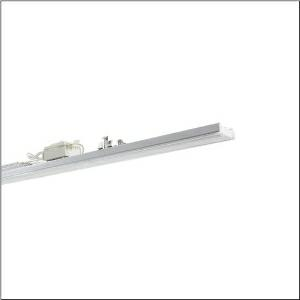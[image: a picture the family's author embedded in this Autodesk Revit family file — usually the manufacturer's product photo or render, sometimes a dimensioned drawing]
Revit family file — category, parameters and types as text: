
# Revit family: licross_21_recessed_mo_52tl127n44xg
name_source: partatom
category: Lighting Fixtures
units: mm (PartAtom-declared; Revit-internal decimal feet)

## family parameters
Cut with Voids When Loaded = No
Host = Face
Light Source = No
Part Type = Normal
Room Calculation Point = No
Round Connector Dimension = Use Diameter
Shared = No

## types (1)
- Licross 21 Recessed MO (1 x LED, 4160 lm, 22.2 W, 4000K)
    Apparent Load = 22 VA
    CIE Flux Codes = 72 92 99 100 100
    Color Rendering = 80
    Color Temperature = 4000K
    Default Elevation = 1800 mm
    Description = Licross 21 Recessed MO, luminaire insert, of sheet steel, galvanised, coil coated, white, length: 1.500mm, width: 66mm, height: 67mm, LED rated luminous flux: 4.160lm, light colour: 840, SDCM (Standard Deviation of Colour Matching)MacAdam ≤ 3 SDCM (initial), control gear: ON/OFF, with plug, 3-pole, with phase selection, mains connection: 220..240V, AC, 50/60Hz, rated input power: 22W, internal wiring halogen-free, primary optical cover: cover, of PMMA, light emission: direct distribution, primary light characteristic: symmetric, protection rating (complete): IP40, insulation class (complete): insulation class I (protective earthing), certification: CE, ENEC, VDE, UKCA, protection symbol: D if used in an environment without relevant dust loads with corresponding accessories, impact resistance: IK06, permissible ambient temperature for indoor applications: -35..+50°C, corresponds to IFS (International Featured Standards) requirements for safety and quality in the food industry, reducing of maximum allowable ambient temperature of 5°C with ceiling mounting, LABS conformity tested according to VDMA 24364:2018-05, The light source and the operating device comply with the requirements of the Ecodesign Regulation (EU) 2019/2020 and are replaceable in accordance with this regulation, packaging unit: 1 piece
    Height = 58 mm
    Lamp = 1 x LED
    Lamp Light Flux = 4160 lm
    Lamp Power = 22.2 W
    Lamp count = 1
    Length = 1500 mm
    Luminous efficacy = 187 lm/W
    Manufacturer = Siteco
    ModVariant = No
    Model = 52TL127N44XG
    Mounting Place = Ceiling
    Mounting Type = Pendant
    Number of Poles = 1
    OnlyDefault = Yes
    Power Factor = 1
    Product Name = Licross 21 Recessed MO
    Product group = luminaire insert | ceiling pendant
    ProductGroupID = 901
    Protection Class = Protection class I
    Protection Degree = IP 40
    RLX_Detail_Level = 1
    RLX_Emergency_Light_Flux = 0 lm
    RLX_Emergency_Type = 0
    RLX_Emergency_Type_DB = No
    RlxData = <blob elided: 21225 chars, md5=3c142461>
    Socket = socket
    Standby Power = 0 W
    System Light Flux = 4160 lm
    System Power = 22 W
    Type Comments = Product without accessories
    Type Image = l_1296930.jpg
    URL = http://relux.com
    VarID = ---
    Voltage = 0 V
    Weight = 0.00 kg
    Width = 66 mm

## geometry (parser evidence)
native form markers: Blend x4, Sweep x9
no freeform markers — native parametric forms only
